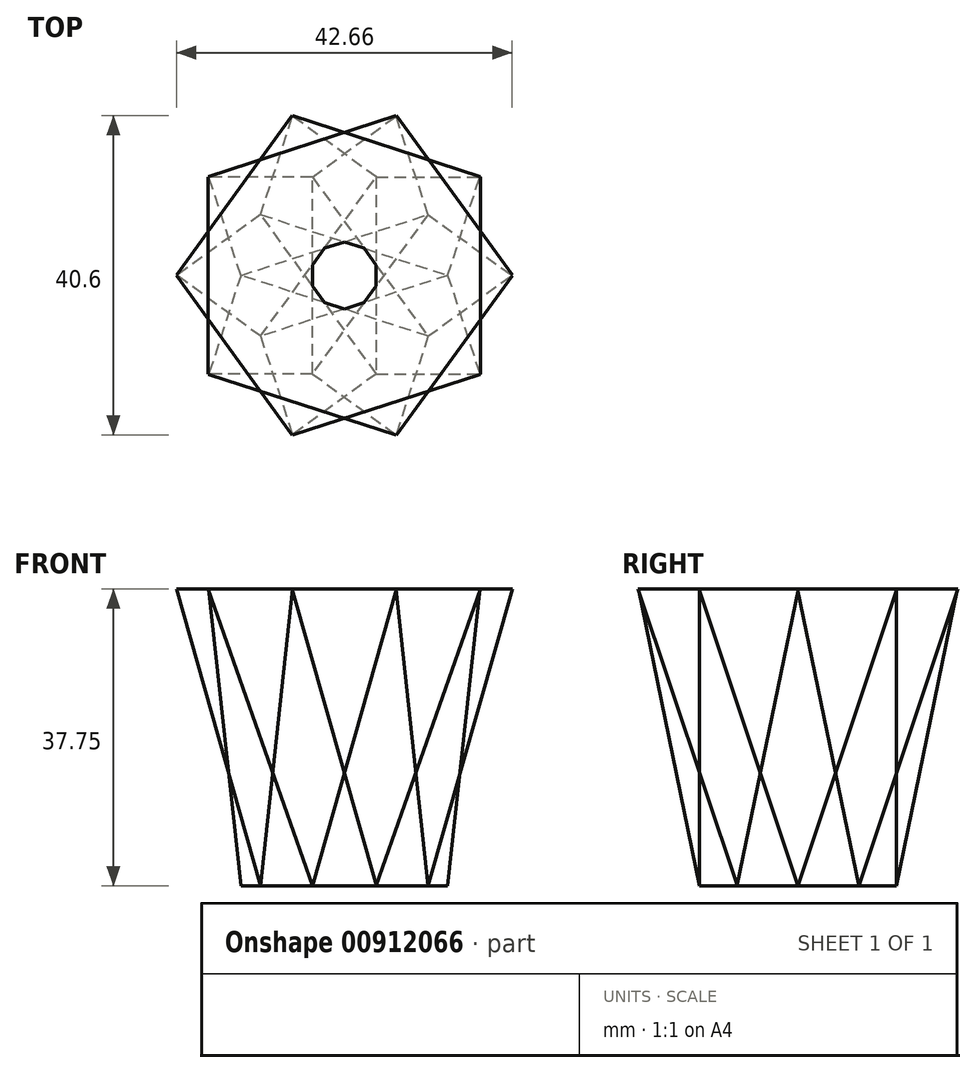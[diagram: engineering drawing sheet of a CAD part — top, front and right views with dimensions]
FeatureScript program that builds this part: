
annotation { "Feature Type Name" : "Feature", "Feature Type Description" : "" }
export const myFeature = defineFeature(function(context is Context, id is Id, definition is map)
    precondition{}
    {
        {
            var Q0;
            Q0=qCreatedBy(makeId("Front.planeOp"),FACE);
            var sketch = newSketch(context, id + "F0", { "sketchPlane" : qUnion([Q0])});
            skLineSegment(sketch, "E0", {"start": v(4.06, 0) * mm, "end": v(17.29, 37.75) * mm});
            skSolve(sketch);
        }
        {
            var Q0;
            Q0=sQuery(id+"F0.wireOp",EDGE,"E0");
            extrude(context, id + "F1", {"bodyType" : ToolBodyType.SURFACE, "surfaceEntities" : qUnion([Q0]), "endBound" : BoundingType.SYMMETRIC, "depth" : 25 * mm, "offsetDistance" : 25 * mm});
        }
        {
            var Q0;
            Q0=qCreatedBy(makeId("Front.planeOp"),FACE);
            var sketch = newSketch(context, id + "F2", { "sketchPlane" : qUnion([Q0])});
            skLineSegment(sketch, "E1", {"start": v(0, 56.15) * mm, "end": v(0, -19) * mm, "construction": true});
            skSolve(sketch);
        }
        {
            var Q0;
            Q0=makeQuery(id+"F1.opExtrude","SWEPT_BODY",BODY,{"disambiguationData":[OSD([sQuery(id+"F0.wireOp",EDGE,"E0")])]});
            var Q1;
            Q1=sQuery(id+"F2.wireOp",EDGE,"E1");
            circularPattern(context, id + "F3", {"entities" : qUnion([Q0]), "axis" : qUnion([Q1]), "angle" : 360 * degree, "instanceCount" : 10, "equalSpace" : true});
        }
    });
